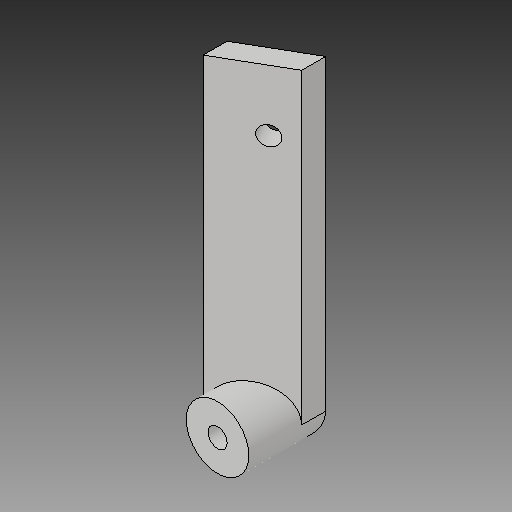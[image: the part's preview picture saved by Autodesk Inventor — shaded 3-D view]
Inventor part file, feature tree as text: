
AUTODESK INVENTOR PART (.ipt)
format: ipt  version: 2018 (Build 220112000, 112)  size: 105,472 bytes
history: native  units: in
note: dims shown in document units (in); Inventor stores cm internally (conversion verified against a paired STEP export)
features: sketch x8, other x3
ambient origin geometry x8: Origin, YZ Plane, XZ Plane, XY Plane, X Axis, Y Axis, Z Axis, Center Point
bodies: Solid1 (feature_tree)
feature tree (11):
  other  "terminal_mount.ipt"
  other  "Solid1::terminal_mount.ipt"
  other  "TaggingFeature1"
  sketch  "Sketch1"  dims[d0=0.3937in]
  sketch  "Sketch2"
  sketch  "Sketch3"
  sketch  "Sketch4"
  sketch  "Sketch5"
  sketch  "Sketch6"
  sketch  "Sketch7"
  sketch  "Sketch9"
